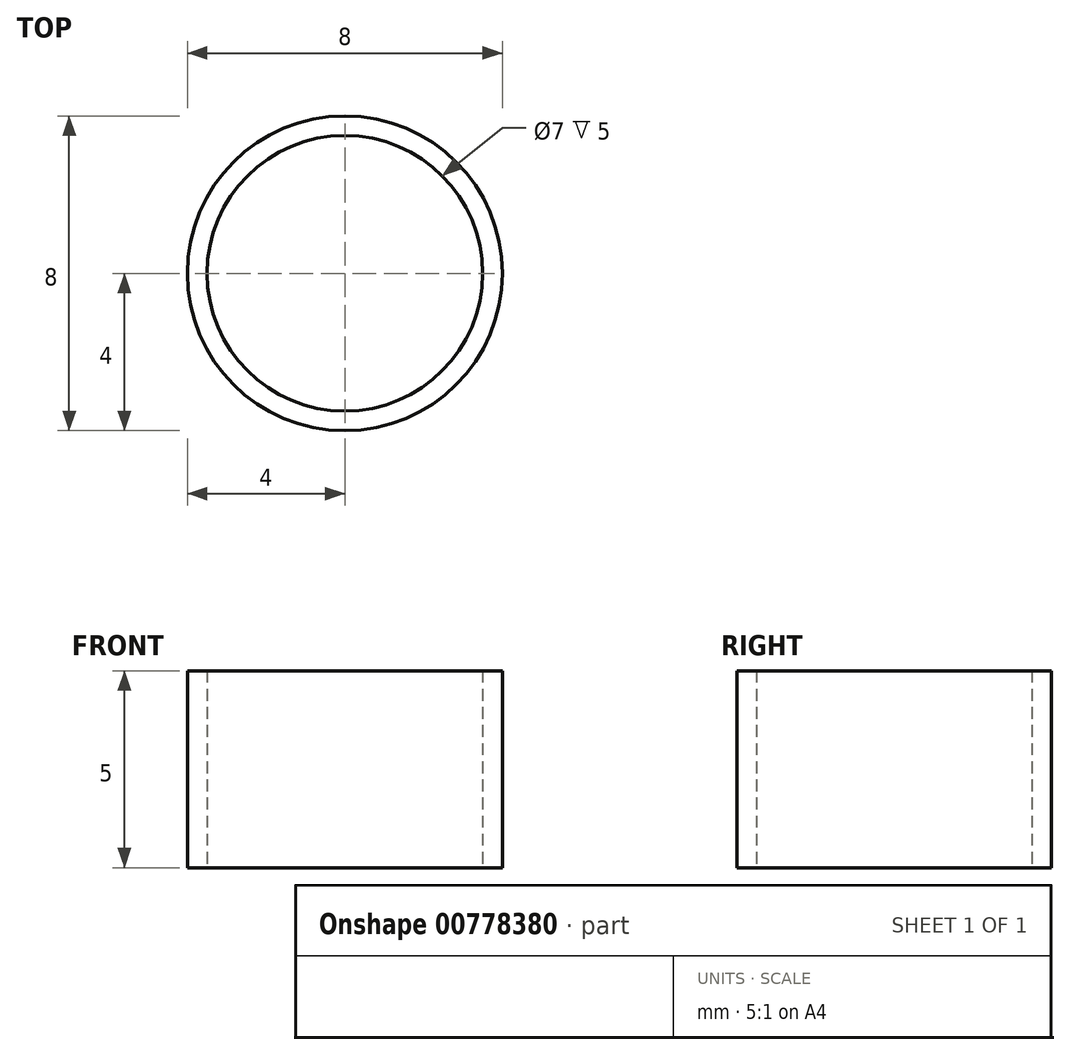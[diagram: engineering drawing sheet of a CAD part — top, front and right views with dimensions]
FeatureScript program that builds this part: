
annotation { "Feature Type Name" : "Feature", "Feature Type Description" : "" }
export const myFeature = defineFeature(function(context is Context, id is Id, definition is map)
    precondition{}
    {
        {
            var Q0;
            Q0=qCreatedBy(makeId("Top.planeOp"),FACE);
            var sketch = newSketch(context, id + "F0", { "sketchPlane" : qUnion([Q0])});
            skCircle(sketch, "E0", {"center": v(0, 0) * mm, "radius": 11 * mm});
            skCircle(sketch, "E1", {"center": v(0, 0) * mm, "radius": 5.5 * mm});
            skCircle(sketch, "E2", {"center": v(0, 0) * mm, "radius": 4 * mm});
            skCircle(sketch, "E3", {"center": v(0, 0) * mm, "radius": 3.5 * mm});
            skSolve(sketch);
        }
        {
            var Q0;
            Q0=makeQuery(id+"F0.imprint","IMPRINT",FACE,{"disambiguationData":[TD([[makeQuery(id+"F0.imprint","IMPRINT",EDGE,{"derivedFrom":sQuery(id+"F0.wireOp",EDGE,"E2")}),1.0]])]});
            extrude(context, id + "F1", {"entities" : qUnion([Q0]), "depth" : 5 * mm, "offsetDistance" : 25 * mm});
        }
    });
